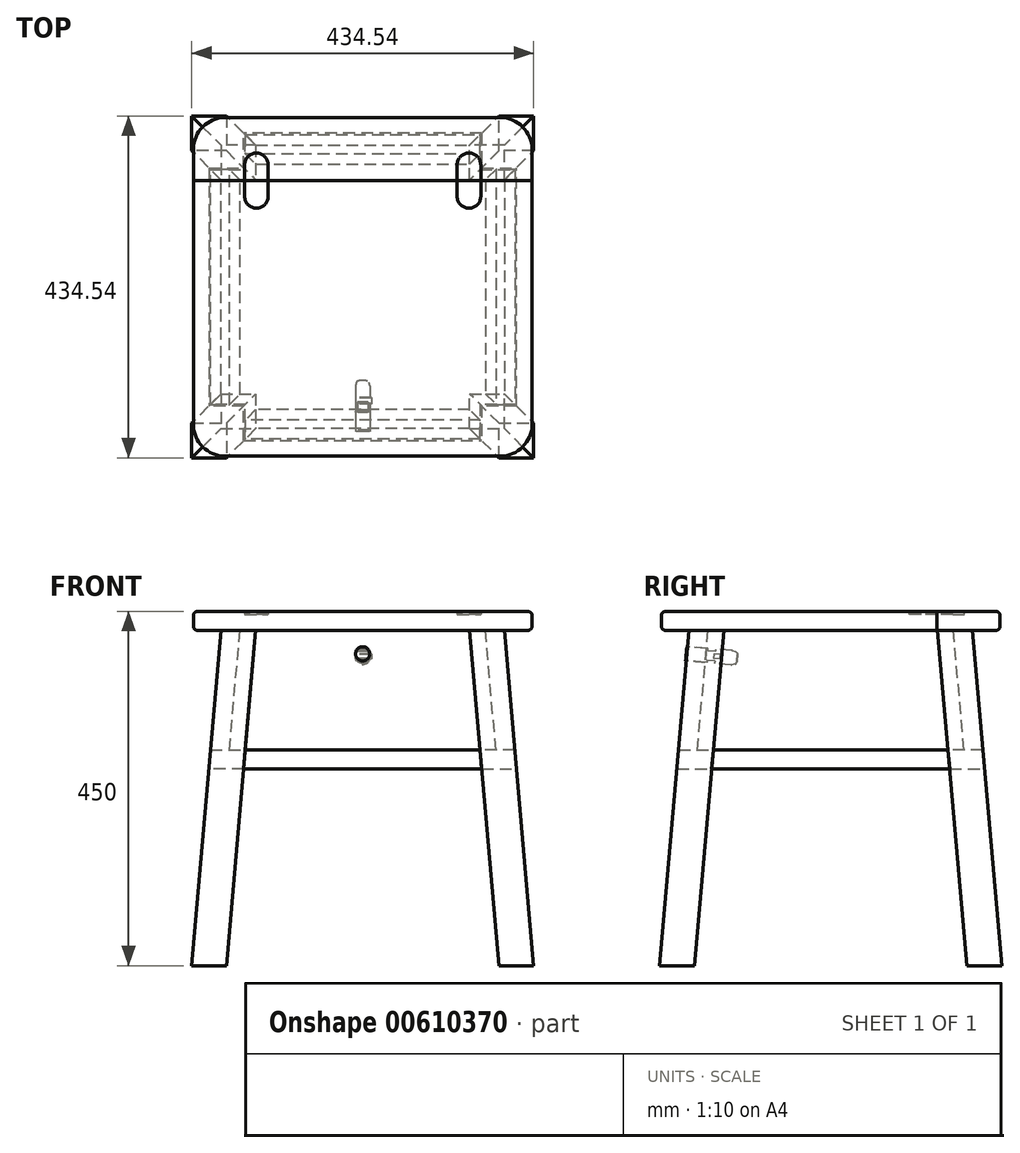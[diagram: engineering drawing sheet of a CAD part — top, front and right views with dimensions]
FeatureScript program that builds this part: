
annotation { "Feature Type Name" : "Feature", "Feature Type Description" : "" }
export const myFeature = defineFeature(function(context is Context, id is Id, definition is map)
    precondition{}
    {
        {
            var Q0;
            Q0=qCreatedBy(makeId("Front.planeOp"),FACE);
            var sketch = newSketch(context, id + "F0", { "sketchPlane" : qUnion([Q0])});
            skLineSegment(sketch, "E0", {"start": v(0, 0) * mm, "end": v(0, 212.68) * mm, "construction": true});
            skSolve(sketch);
        }
        {
            var Q0;
            Q0=qCreatedBy(makeId("Right.planeOp"),FACE);
            var sketch = newSketch(context, id + "F1", { "sketchPlane" : qUnion([Q0])});
            skLineSegment(sketch, "E1", {"start": v(173.1, -450) * mm, "end": v(135.83, -24) * mm});
            skLineSegment(sketch, "E2", {"start": v(135.83, -24) * mm, "end": v(180, -24) * mm});
            skLineSegment(sketch, "E3", {"start": v(180, -24) * mm, "end": v(217.27, -450) * mm});
            skLineSegment(sketch, "E4", {"start": v(217.27, -450) * mm, "end": v(173.1, -450) * mm});
            skSolve(sketch);
        }
        {
            var Q0;
            Q0=makeQuery(id+"F1.imprint","IMPRINT",FACE,{"disambiguationData":[TD([[makeQuery(id+"F1.imprint","IMPRINT",EDGE,{"derivedFrom":sQuery(id+"F1.wireOp",EDGE,"E1")}),-1.0]])]});
            extrude(context, id + "F2", {"entities" : qUnion([Q0]), "flatOperationType" : FlatOperationType.REMOVE, "endBound" : BoundingType.SYMMETRIC, "depth" : 800 * mm, "offsetDistance" : 25 * mm, "domain" : OperationDomain.MODEL});
        }
        {
            var Q0;
            Q0=makeQuery(id+"F2.opExtrude","SWEPT_BODY",BODY,{"disambiguationData":[OSD([sQuery(id+"F1.wireOp",EDGE,"E1"),sQuery(id+"F1.wireOp",EDGE,"E2"),sQuery(id+"F1.wireOp",EDGE,"E3"),sQuery(id+"F1.wireOp",EDGE,"E4")])]});
            var Q1;
            Q1=sQuery(id+"F0.wireOp",EDGE,"E0");
            circularPattern(context, id + "F3", {"entities" : qUnion([Q0]), "axis" : qUnion([Q1]), "angle" : 90 * degree, "instanceCount" : 2, "equalSpace" : true});
        }
        {
            var Q0;
            Q0=makeQuery(id+"F2.opExtrude","SWEPT_BODY",BODY,{"disambiguationData":[OSD([sQuery(id+"F1.wireOp",EDGE,"E1"),sQuery(id+"F1.wireOp",EDGE,"E2"),sQuery(id+"F1.wireOp",EDGE,"E3"),sQuery(id+"F1.wireOp",EDGE,"E4")])]});
            var Q1;
            Q1=makeQuery(id+"F3.opPattern","COPY",BODY,{"derivedFrom":makeQuery(id+"F2.opExtrude","SWEPT_BODY",BODY,{"disambiguationData":[OSD([sQuery(id+"F1.wireOp",EDGE,"E1"),sQuery(id+"F1.wireOp",EDGE,"E2"),sQuery(id+"F1.wireOp",EDGE,"E3"),sQuery(id+"F1.wireOp",EDGE,"E4")])]}),"instanceName":"1"});
            booleanBodies(context, id + "F4", {"operationType" : BooleanOperationType.INTERSECTION, "tools" : qUnion([Q0, Q1])});
        }
        {
            var Q0;
            {var subQ0=makeQuery(id+"F2.opExtrude","SWEPT_BODY",BODY,{"disambiguationData":[OSD([sQuery(id+"F1.wireOp",EDGE,"E1"),sQuery(id+"F1.wireOp",EDGE,"E2"),sQuery(id+"F1.wireOp",EDGE,"E3"),sQuery(id+"F1.wireOp",EDGE,"E4")])]});Q0=makeQuery(id+"F4.opBoolean","INTERSECT",BODY,{"derivedFrom":[subQ0,makeQuery(id+"F3.opPattern","COPY",BODY,{"derivedFrom":subQ0,"instanceName":"1"})]});}
            var Q1;
            Q1=sQuery(id+"F0.wireOp",EDGE,"E0");
            circularPattern(context, id + "F5", {"entities" : qUnion([Q0]), "axis" : qUnion([Q1]), "angle" : 360 * degree, "instanceCount" : 4, "equalSpace" : true});
        }
        {
            var Q0;
            Q0=qCreatedBy(makeId("Top.planeOp"),FACE);
            var sketch = newSketch(context, id + "F6", { "sketchPlane" : qUnion([Q0])});
            skLineSegment(sketch, "E5.bottom", {"start": v(-177.9, -177.9) * mm, "end": v(177.9, -177.9) * mm});
            skLineSegment(sketch, "E5.top", {"start": v(-177.9, 177.9) * mm, "end": v(177.9, 177.9) * mm});
            skLineSegment(sketch, "E5.left", {"start": v(-177.9, -177.9) * mm, "end": v(-177.9, 177.9) * mm});
            skLineSegment(sketch, "E5.right", {"start": v(177.9, -177.9) * mm, "end": v(177.9, 177.9) * mm});
            skSolve(sketch);
        }
        {
            var Q0;
            Q0=makeQuery(id+"F6.imprint","IMPRINT",FACE,{"disambiguationData":[TD([[makeQuery(id+"F6.imprint","IMPRINT",EDGE,{"derivedFrom":sQuery(id+"F6.wireOp",EDGE,"E5.bottom")}),1.0]])]});
            extrude(context, id + "F7", {"entities" : qUnion([Q0]), "oppositeDirection" : true, "depth" : 200 * mm, "offsetDistance" : 25 * mm, "hasDraft" : true, "draftAngle" : 5 * degree, "hasSecondDirection" : true, "secondDirectionOppositeDirection" : true, "secondDirectionDepth" : 176 * mm});
        }
        {
            var Q0;
            {var subQ0=makeQuery(id+"F2.opExtrude","SWEPT_BODY",BODY,{"disambiguationData":[OSD([sQuery(id+"F1.wireOp",EDGE,"E1"),sQuery(id+"F1.wireOp",EDGE,"E2"),sQuery(id+"F1.wireOp",EDGE,"E3"),sQuery(id+"F1.wireOp",EDGE,"E4")])]});Q0=makeQuery(id+"F5.opPattern","COPY",BODY,{"derivedFrom":makeQuery(id+"F4.opBoolean","INTERSECT",BODY,{"derivedFrom":[subQ0,makeQuery(id+"F3.opPattern","COPY",BODY,{"derivedFrom":subQ0,"instanceName":"1"})]}),"instanceName":"2"});}
            var Q1;
            {var subQ0=makeQuery(id+"F2.opExtrude","SWEPT_BODY",BODY,{"disambiguationData":[OSD([sQuery(id+"F1.wireOp",EDGE,"E1"),sQuery(id+"F1.wireOp",EDGE,"E2"),sQuery(id+"F1.wireOp",EDGE,"E3"),sQuery(id+"F1.wireOp",EDGE,"E4")])]});Q1=makeQuery(id+"F5.opPattern","COPY",BODY,{"derivedFrom":makeQuery(id+"F4.opBoolean","INTERSECT",BODY,{"derivedFrom":[subQ0,makeQuery(id+"F3.opPattern","COPY",BODY,{"derivedFrom":subQ0,"instanceName":"1"})]}),"instanceName":"3"});}
            var Q2;
            {var subQ0=makeQuery(id+"F2.opExtrude","SWEPT_BODY",BODY,{"disambiguationData":[OSD([sQuery(id+"F1.wireOp",EDGE,"E1"),sQuery(id+"F1.wireOp",EDGE,"E2"),sQuery(id+"F1.wireOp",EDGE,"E3"),sQuery(id+"F1.wireOp",EDGE,"E4")])]});Q2=makeQuery(id+"F4.opBoolean","INTERSECT",BODY,{"derivedFrom":[subQ0,makeQuery(id+"F3.opPattern","COPY",BODY,{"derivedFrom":subQ0,"instanceName":"1"})]});}
            var Q3;
            {var subQ0=makeQuery(id+"F2.opExtrude","SWEPT_BODY",BODY,{"disambiguationData":[OSD([sQuery(id+"F1.wireOp",EDGE,"E1"),sQuery(id+"F1.wireOp",EDGE,"E2"),sQuery(id+"F1.wireOp",EDGE,"E3"),sQuery(id+"F1.wireOp",EDGE,"E4")])]});Q3=makeQuery(id+"F5.opPattern","COPY",BODY,{"derivedFrom":makeQuery(id+"F4.opBoolean","INTERSECT",BODY,{"derivedFrom":[subQ0,makeQuery(id+"F3.opPattern","COPY",BODY,{"derivedFrom":subQ0,"instanceName":"1"})]}),"instanceName":"1"});}
            var Q4;
            Q4=makeQuery(id+"F7.opExtrude","SWEPT_BODY",BODY,{"disambiguationData":[OSD([sQuery(id+"F6.wireOp",EDGE,"E5.bottom"),sQuery(id+"F6.wireOp",EDGE,"E5.top"),sQuery(id+"F6.wireOp",EDGE,"E5.left"),sQuery(id+"F6.wireOp",EDGE,"E5.right")])]});
            booleanBodies(context, id + "F8", {"operationType" : BooleanOperationType.SUBTRACTION, "tools" : qUnion([Q0, Q1, Q2, Q3]), "targets" : qUnion([Q4]), "keepTools" : true});
        }
        {
            var Q0;
            Q0=qCreatedBy(makeId("Top.planeOp"),FACE);
            var sketch = newSketch(context, id + "F9", { "sketchPlane" : qUnion([Q0])});
            skLineSegment(sketch, "E6.bottom", {"start": v(-175, 215) * mm, "end": v(175, 215) * mm});
            skLineSegment(sketch, "E6.top", {"start": v(-175, -215) * mm, "end": v(175, -215) * mm});
            skLineSegment(sketch, "E6.left", {"start": v(-215, 175) * mm, "end": v(-215, -175) * mm});
            skLineSegment(sketch, "E6.right", {"start": v(215, 175) * mm, "end": v(215, 135) * mm});
            skPoint(sketch, "E7.visualSharp", {"position": v(-215, -215) * mm});
            skArc(sketch, "E7.filletArc", {"start": v(-215, -175) * mm, "mid": v(-203.28, -203.28) * mm, "end": v(-175, -215) * mm});
            skPoint(sketch, "E8.visualSharp", {"position": v(-215, 215) * mm});
            skArc(sketch, "E8.filletArc", {"start": v(-175, 215) * mm, "mid": v(-203.28, 203.28) * mm, "end": v(-215, 175) * mm});
            skPoint(sketch, "E9.visualSharp", {"position": v(215, -215) * mm});
            skArc(sketch, "E9.filletArc", {"start": v(175, -215) * mm, "mid": v(203.28, -203.28) * mm, "end": v(215, -175) * mm});
            skPoint(sketch, "E10.visualSharp", {"position": v(215, 215) * mm});
            skArc(sketch, "E10.filletArc", {"start": v(215, 175) * mm, "mid": v(203.28, 203.28) * mm, "end": v(175, 215) * mm});
            skLineSegment(sketch, "E11", {"start": v(-215, 135) * mm, "end": v(-215, 135) * mm});
            skLineSegment(sketch, "E12", {"start": v(-215, 135) * mm, "end": v(215, 135) * mm});
            skLineSegment(sketch, "E13", {"start": v(215, 135) * mm, "end": v(215, -175) * mm});
            skSolve(sketch);
        }
        {
            var Q0;
            Q0=makeQuery(id+"F9.imprint","IMPRINT",FACE,{"disambiguationData":[TD([[makeQuery(id+"F9.imprint","IMPRINT",EDGE,{"derivedFrom":sQuery(id+"F9.wireOp",EDGE,"E6.bottom")}),-1.0]])]});
            extrude(context, id + "F10", {"entities" : qUnion([Q0]), "oppositeDirection" : true, "depth" : 24 * mm, "offsetDistance" : 25 * mm});
        }
        {
            var Q0;
            Q0=makeQuery(id+"F10.opExtrude","CAP_EDGE",EDGE,{"disambiguationData":[OSD([sQuery(id+"F9.wireOp",EDGE,"E8.filletArc")])],"isStart":true});
            var Q1;
            Q1=makeQuery(id+"F10.opExtrude","CAP_EDGE",EDGE,{"disambiguationData":[OSD([sQuery(id+"F9.wireOp",EDGE,"E8.filletArc")])],"isStart":false});
            fillet(context, id + "F11", {"entities" : qUnion([Q0, Q1]), "radius" : 5 * mm, "tangentPropagation" : true, "allowEdgeOverflow" : false});
        }
        {
            var Q0;
            Q0=makeQuery(id+"F9.imprint","IMPRINT",FACE,{"disambiguationData":[TD([[makeQuery(id+"F9.imprint","IMPRINT",EDGE,{"derivedFrom":sQuery(id+"F9.wireOp",EDGE,"E6.top")}),1.0]])]});
            extrude(context, id + "F12", {"entities" : qUnion([Q0]), "oppositeDirection" : true, "depth" : 24 * mm, "offsetDistance" : 25 * mm});
        }
        {
            var Q0;
            Q0=makeQuery(id+"F12.opExtrude","SWEPT_FACE",FACE,{"disambiguationData":[OSD([sQuery(id+"F9.wireOp",EDGE,"E9.filletArc")])]});
            fillet(context, id + "F13", {"entities" : qUnion([Q0]), "radius" : 5 * mm, "tangentPropagation" : true, "allowEdgeOverflow" : false});
        }
        {
            var Q0;
            Q0=qCreatedBy(makeId("Front.planeOp"),FACE);
            var sketch = newSketch(context, id + "F14", { "sketchPlane" : qUnion([Q0])});
            skLineSegment(sketch, "E14.bottom", {"start": v(-155.9, -24) * mm, "end": v(-180, -24) * mm});
            skLineSegment(sketch, "E14.top", {"start": v(-169.2, -176) * mm, "end": v(-193.3, -176) * mm});
            skLineSegment(sketch, "E14.left", {"start": v(-155.9, -24) * mm, "end": v(-169.2, -176) * mm});
            skLineSegment(sketch, "E14.right", {"start": v(-180, -24) * mm, "end": v(-193.3, -176) * mm});
            skSolve(sketch);
        }
        {
            var Q0;
            Q0=makeQuery(id+"F14.imprint","IMPRINT",FACE,{"disambiguationData":[TD([[makeQuery(id+"F14.imprint","IMPRINT",EDGE,{"derivedFrom":sQuery(id+"F14.wireOp",EDGE,"E14.bottom")}),1.0]])]});
            extrude(context, id + "F15", {"entities" : qUnion([Q0]), "endBound" : BoundingType.UP_TO_NEXT, "depth" : 25 * mm, "offsetDistance" : 25 * mm, "hasSecondDirection" : true, "secondDirectionBound" : SecondDirectionBoundingType.UP_TO_NEXT, "secondDirectionOppositeDirection" : true, "secondDirectionDepth" : 25 * mm});
        }
        {
            var Q0;
            Q0=makeQuery(id+"F15.opExtrude","SWEPT_BODY",BODY,{"disambiguationData":[OSD([sQuery(id+"F14.wireOp",EDGE,"E14.bottom"),sQuery(id+"F14.wireOp",EDGE,"E14.top"),sQuery(id+"F14.wireOp",EDGE,"E14.left"),sQuery(id+"F14.wireOp",EDGE,"E14.right")])]});
            var Q1;
            Q1=sQuery(id+"F0.wireOp",EDGE,"E0");
            circularPattern(context, id + "F16", {"entities" : qUnion([Q0]), "axis" : qUnion([Q1]), "angle" : 360 * degree, "instanceCount" : 4, "equalSpace" : true});
        }
        {
            var Q0;
            Q0=qCreatedBy(makeId("Top.planeOp"),FACE);
            var sketch = newSketch(context, id + "F17", { "sketchPlane" : qUnion([Q0])});
            skLineSegment(sketch, "E15.left", {"start": v(-150, 155) * mm, "end": v(-150, 115) * mm});
            skLineSegment(sketch, "E15.right", {"start": v(-120, 155) * mm, "end": v(-120, 115) * mm});
            skArc(sketch, "E16", {"start": v(-150, 115) * mm, "mid": v(-135, 100) * mm, "end": v(-120, 115) * mm});
            skArc(sketch, "E17", {"start": v(-120, 155) * mm, "mid": v(-135, 170) * mm, "end": v(-150, 155) * mm});
            skLineSegment(sketch, "E18.MirrorCS", {"start": v(120, 155) * mm, "end": v(120, 115) * mm});
            skArc(sketch, "E19.MirrorCS", {"start": v(150, 115) * mm, "mid": v(135, 100) * mm, "end": v(120, 115) * mm});
            skLineSegment(sketch, "E20.MirrorCS", {"start": v(150, 155) * mm, "end": v(150, 115) * mm});
            skArc(sketch, "E21.MirrorCS", {"start": v(120, 155) * mm, "mid": v(135, 170) * mm, "end": v(150, 155) * mm});
            skSolve(sketch);
        }
        {
            var Q0;
            Q0=makeQuery(id+"F17.imprint","IMPRINT",FACE,{"disambiguationData":[TD([[makeQuery(id+"F17.imprint","IMPRINT",EDGE,{"derivedFrom":sQuery(id+"F17.wireOp",EDGE,"E15.left")}),1.0]])]});
            var Q1;
            Q1=makeQuery(id+"F17.imprint","IMPRINT",FACE,{"disambiguationData":[TD([[makeQuery(id+"F17.imprint","IMPRINT",EDGE,{"derivedFrom":sQuery(id+"F17.wireOp",EDGE,"E18.MirrorCS")}),1.0]])]});
            extrude(context, id + "F18", {"entities" : qUnion([Q0, Q1]), "oppositeDirection" : true, "depth" : 4 * mm, "offsetDistance" : 25 * mm});
        }
        {
            var Q0;
            Q0=makeQuery(id+"F18.opExtrude","SWEPT_BODY",BODY,{"disambiguationData":[OSD([sQuery(id+"F17.wireOp",EDGE,"E15.left"),sQuery(id+"F17.wireOp",EDGE,"E15.right"),sQuery(id+"F17.wireOp",EDGE,"E16"),sQuery(id+"F17.wireOp",EDGE,"E17")])]});
            var Q1;
            Q1=makeQuery(id+"F18.opExtrude","SWEPT_BODY",BODY,{"disambiguationData":[OSD([sQuery(id+"F17.wireOp",EDGE,"E18.MirrorCS"),sQuery(id+"F17.wireOp",EDGE,"E19.MirrorCS"),sQuery(id+"F17.wireOp",EDGE,"E20.MirrorCS"),sQuery(id+"F17.wireOp",EDGE,"E21.MirrorCS")])]});
            var Q2;
            Q2=makeQuery(id+"F10.opExtrude","SWEPT_BODY",BODY,{"disambiguationData":[OSD([sQuery(id+"F9.wireOp",EDGE,"E6.bottom"),sQuery(id+"F9.wireOp",EDGE,"E6.left"),sQuery(id+"F9.wireOp",EDGE,"E6.right"),sQuery(id+"F9.wireOp",EDGE,"E8.filletArc"),sQuery(id+"F9.wireOp",EDGE,"E10.filletArc"),sQuery(id+"F9.wireOp",EDGE,"E12")])]});
            var Q3;
            Q3=makeQuery(id+"F12.opExtrude","SWEPT_BODY",BODY,{"disambiguationData":[OSD([sQuery(id+"F9.wireOp",EDGE,"E6.top"),sQuery(id+"F9.wireOp",EDGE,"E6.left"),sQuery(id+"F9.wireOp",EDGE,"E7.filletArc"),sQuery(id+"F9.wireOp",EDGE,"E9.filletArc"),sQuery(id+"F9.wireOp",EDGE,"E12"),sQuery(id+"F9.wireOp",EDGE,"E13")])]});
            booleanBodies(context, id + "F19", {"operationType" : BooleanOperationType.SUBTRACTION, "tools" : qUnion([Q0, Q1]), "targets" : qUnion([Q2, Q3])});
        }
        {
            var Q0;
            Q0=makeQuery(id+"F16.opPattern","COPY",FACE,{"derivedFrom":makeQuery(id+"F15.opExtrude","SWEPT_FACE",FACE,{"disambiguationData":[OSD([sQuery(id+"F14.wireOp",EDGE,"E14.right")])]}),"instanceName":"1"});
            var sketch = newSketch(context, id + "F20", { "sketchPlane" : qUnion([Q0])});
            skPoint(sketch, "E22", {"position": v(0, -69.6) * mm});
            skLineSegment(sketch, "E23", {"start": v(0, -39.6) * mm, "end": v(0, -127.9) * mm});
            skSolve(sketch);
        }
        {
            var Q0;
            Q0=sQuery(id+"F20.wireOp",VERTEX,"E22");
            var Q1;
            Q1=makeQuery(id+"F16.opPattern","COPY",BODY,{"derivedFrom":makeQuery(id+"F15.opExtrude","SWEPT_BODY",BODY,{"disambiguationData":[OSD([sQuery(id+"F14.wireOp",EDGE,"E14.bottom"),sQuery(id+"F14.wireOp",EDGE,"E14.top"),sQuery(id+"F14.wireOp",EDGE,"E14.left"),sQuery(id+"F14.wireOp",EDGE,"E14.right")])]}),"instanceName":"1"});
            hole(context, id + "F21", {"style" : HoleStyle.SIMPLE, "endStyle" : HoleEndStyle.THROUGH, "holeDiameter" : 18 * mm, "majorDiameter" : 5 * mm, "isTappedThrough" : true, "tappedDepth" : 12 * mm, "tapClearance" : 3, "startFromSketch" : true, "locations" : qUnion([Q0]), "scope" : qUnion([Q1])});
        }
        {
            var Q0;
            Q0=makeQuery(id+"F16.opPattern","COPY",FACE,{"derivedFrom":makeQuery(id+"F15.opExtrude","SWEPT_FACE",FACE,{"disambiguationData":[OSD([sQuery(id+"F14.wireOp",EDGE,"E14.left")])]}),"instanceName":"1"});
            cPlane(context, id + "F22", {"entities" : qUnion([Q0]), "cplaneType" : CPlaneType.OFFSET, "offset" : 10 * mm, "width" : 150 * mm, "height" : 150 * mm});
        }
        {
            var Q0;
            Q0=qCreatedBy(id+"F22.planeOp",FACE);
            var sketch = newSketch(context, id + "F23", { "sketchPlane" : qUnion([Q0])});
            skLineSegment(sketch, "E24.bottom", {"start": v(-11, -66.6) * mm, "end": v(9, -66.6) * mm});
            skLineSegment(sketch, "E24.top", {"start": v(-11, -72.6) * mm, "end": v(9, -72.6) * mm});
            skLineSegment(sketch, "E24.left", {"start": v(-11, -66.6) * mm, "end": v(-11, -72.6) * mm});
            skLineSegment(sketch, "E24.right", {"start": v(9, -66.6) * mm, "end": v(9, -72.6) * mm});
            skLineSegment(sketch, "E25", {"start": v(0, -55.19) * mm, "end": v(0, -93.57) * mm});
            skPoint(sketch, "E26", {"position": v(0, -69.6) * mm});
            skSolve(sketch);
        }
        {
            var Q0;
            {var subQ0=sQuery(id+"F23.wireOp",EDGE,"E24.right");Q0=makeQuery(id+"F23.imprint","IMPRINT",FACE,{"disambiguationData":[TD([[makeQuery(id+"F23.imprint","IMPRINT",EDGE,{"derivedFrom":subQ0}),-1.0]])]});}
            var Q1;
            {var subQ0=sQuery(id+"F23.wireOp",EDGE,"E24.left");Q1=makeQuery(id+"F23.imprint","IMPRINT",FACE,{"disambiguationData":[TD([[makeQuery(id+"F23.imprint","IMPRINT",EDGE,{"derivedFrom":subQ0}),1.0]])]});}
            extrude(context, id + "F24", {"entities" : qUnion([Q0, Q1]), "depth" : 8 * mm, "offsetDistance" : 25 * mm});
        }
        {
            var Q0;
            Q0=qCreatedBy(id+"F22.planeOp",FACE);
            var sketch = newSketch(context, id + "F25", { "sketchPlane" : qUnion([Q0])});
            skLineSegment(sketch, "E27", {"start": v(-6, -92.6) * mm, "end": v(-6, -52.6) * mm});
            skLineSegment(sketch, "E28", {"start": v(26, -92.6) * mm, "end": v(6, -92.6) * mm});
            skLineSegment(sketch, "E29", {"start": v(-26, -42.6) * mm, "end": v(-26, -92.6) * mm});
            skPoint(sketch, "E30.end.orphan", {"position": v(-17, -72.6) * mm});
            skPoint(sketch, "E31.end.orphan", {"position": v(-17, -88.22) * mm});
            skLineSegment(sketch, "E32", {"start": v(26, -42.6) * mm, "end": v(-26, -42.6) * mm});
            skLineSegment(sketch, "E33.MirrorCS", {"start": v(6, -92.6) * mm, "end": v(6, -52.6) * mm});
            skLineSegment(sketch, "E34.MirrorCS", {"start": v(26, -42.6) * mm, "end": v(26, -92.6) * mm});
            skPoint(sketch, "E35.orphan", {"position": v(-6, -92.6) * mm});
            skPoint(sketch, "E36.orphan", {"position": v(6, -92.6) * mm});
            skPoint(sketch, "E37.orphan", {"position": v(6, -72.6) * mm});
            skLineSegment(sketch, "E38.trimOffspring", {"start": v(-6, -52.6) * mm, "end": v(6, -52.6) * mm});
            skLineSegment(sketch, "E39.trimOffspring", {"start": v(-6, -92.6) * mm, "end": v(-26, -92.6) * mm});
            skPoint(sketch, "E40.end.orphan", {"position": v(-6, -72.6) * mm});
            skSolve(sketch);
        }
        {
            var Q0;
            Q0=makeQuery(id+"F25.imprint","IMPRINT",FACE,{"disambiguationData":[TD([[makeQuery(id+"F25.imprint","IMPRINT",EDGE,{"derivedFrom":sQuery(id+"F25.wireOp",EDGE,"E27")}),1.0]])]});
            extrude(context, id + "F26", {"entities" : qUnion([Q0]), "depth" : 2 * mm, "offsetDistance" : 25 * mm, "hasSecondDirection" : true, "secondDirectionOppositeDirection" : true, "secondDirectionDepth" : 8 * mm});
        }
        {
            var Q0;
            Q0=qCreatedBy(id+"F22.planeOp",FACE);
            var sketch = newSketch(context, id + "F27", { "sketchPlane" : qUnion([Q0])});
            skCircle(sketch, "E41", {"center": v(0, -69.6) * mm, "radius": 9 * mm});
            skSolve(sketch);
        }
        {
            var Q0;
            Q0 = qSketchRegion(id + "F27", true);
            extrude(context, id + "F28", {"entities" : qUnion([Q0]), "depth" : 30 * mm, "offsetDistance" : 25 * mm, "hasSecondDirection" : true, "secondDirectionOppositeDirection" : true, "secondDirectionDepth" : 35 * mm});
        }
        {
            var Q0;
            Q0=makeQuery(id+"F28.opExtrude","CAP_EDGE",EDGE,{"disambiguationData":[OSD([sQuery(id+"F27.wireOp",EDGE,"E41")])],"isStart":false});
            chamfer(context, id + "F29", {"entities" : qUnion([Q0]), "chamferType" : ChamferType.TWO_OFFSETS, "width1" : 2 * mm, "oppositeDirection" : false, "width2" : 7 * mm, "tangentPropagation" : true});
        }
        {
            var Q0;
            {var subQ0=sQuery(id+"F27.wireOp",EDGE,"E41");Q0=makeQuery(id+"F29.opChamfer","BLEND_EDGE",EDGE,{"blendedFrom":[makeQuery(id+"F28.opExtrude","CAP_EDGE",EDGE,{"disambiguationData":[OSD([subQ0])],"isStart":false}),makeQuery(id+"F28.opExtrude","SWEPT_FACE",FACE,{"disambiguationData":[OSD([subQ0])]})],"blendedInto":[makeQuery(id+"F28.opExtrude","SWEPT_FACE",FACE,{"disambiguationData":[OSD([subQ0])]})]});}
            var Q1;
            {var subQ0=sQuery(id+"F27.wireOp",EDGE,"E41");Q1=makeQuery(id+"F29.opChamfer","BLEND_EDGE",EDGE,{"blendedFrom":[makeQuery(id+"F28.opExtrude","CAP_EDGE",EDGE,{"disambiguationData":[OSD([subQ0])],"isStart":false}),makeQuery(id+"F28.opExtrude","CAP_FACE",FACE,{"disambiguationData":[OSD([subQ0])],"isStart":false})],"blendedInto":[makeQuery(id+"F28.opExtrude","CAP_FACE",FACE,{"disambiguationData":[OSD([subQ0])],"isStart":false})]});}
            fillet(context, id + "F30", {"entities" : qUnion([Q0, Q1]), "radius" : 3 * mm, "tangentPropagation" : true, "allowEdgeOverflow" : false});
        }
        {
            var Q0;
            Q0=makeQuery(id+"F26.opExtrude","SWEPT_BODY",BODY,{"disambiguationData":[OSD([sQuery(id+"F25.wireOp",EDGE,"E27"),sQuery(id+"F25.wireOp",EDGE,"E28"),sQuery(id+"F25.wireOp",EDGE,"E29"),sQuery(id+"F25.wireOp",EDGE,"E32"),sQuery(id+"F25.wireOp",EDGE,"E33.MirrorCS"),sQuery(id+"F25.wireOp",EDGE,"E34.MirrorCS"),sQuery(id+"F25.wireOp",EDGE,"E38.trimOffspring"),sQuery(id+"F25.wireOp",EDGE,"E39.trimOffspring")])]});
            var Q1;
            Q1=makeQuery(id+"F28.opExtrude","SWEPT_BODY",BODY,{"disambiguationData":[OSD([sQuery(id+"F27.wireOp",EDGE,"E41")])]});
            booleanBodies(context, id + "F31", {"operationType" : BooleanOperationType.SUBTRACTION, "tools" : qUnion([Q0]), "targets" : qUnion([Q1])});
        }
        {
            var Q0;
            Q0=makeQuery(id+"F28.opExtrude","SWEPT_BODY",BODY,{"disambiguationData":[OSD([sQuery(id+"F27.wireOp",EDGE,"E41")])]});
            var Q1;
            Q1=makeQuery(id+"F28.opExtrude","SWEPT_FACE",FACE,{"disambiguationData":[OSD([sQuery(id+"F27.wireOp",EDGE,"E41")])]});
            transform(context, id + "F32", {"entities" : qUnion([Q0]), "transformType" : TransformType.ROTATION, "transformAxis" : qUnion([Q1]), "angle" : 90 * degree, "makeCopy" : false});
        }
    });
